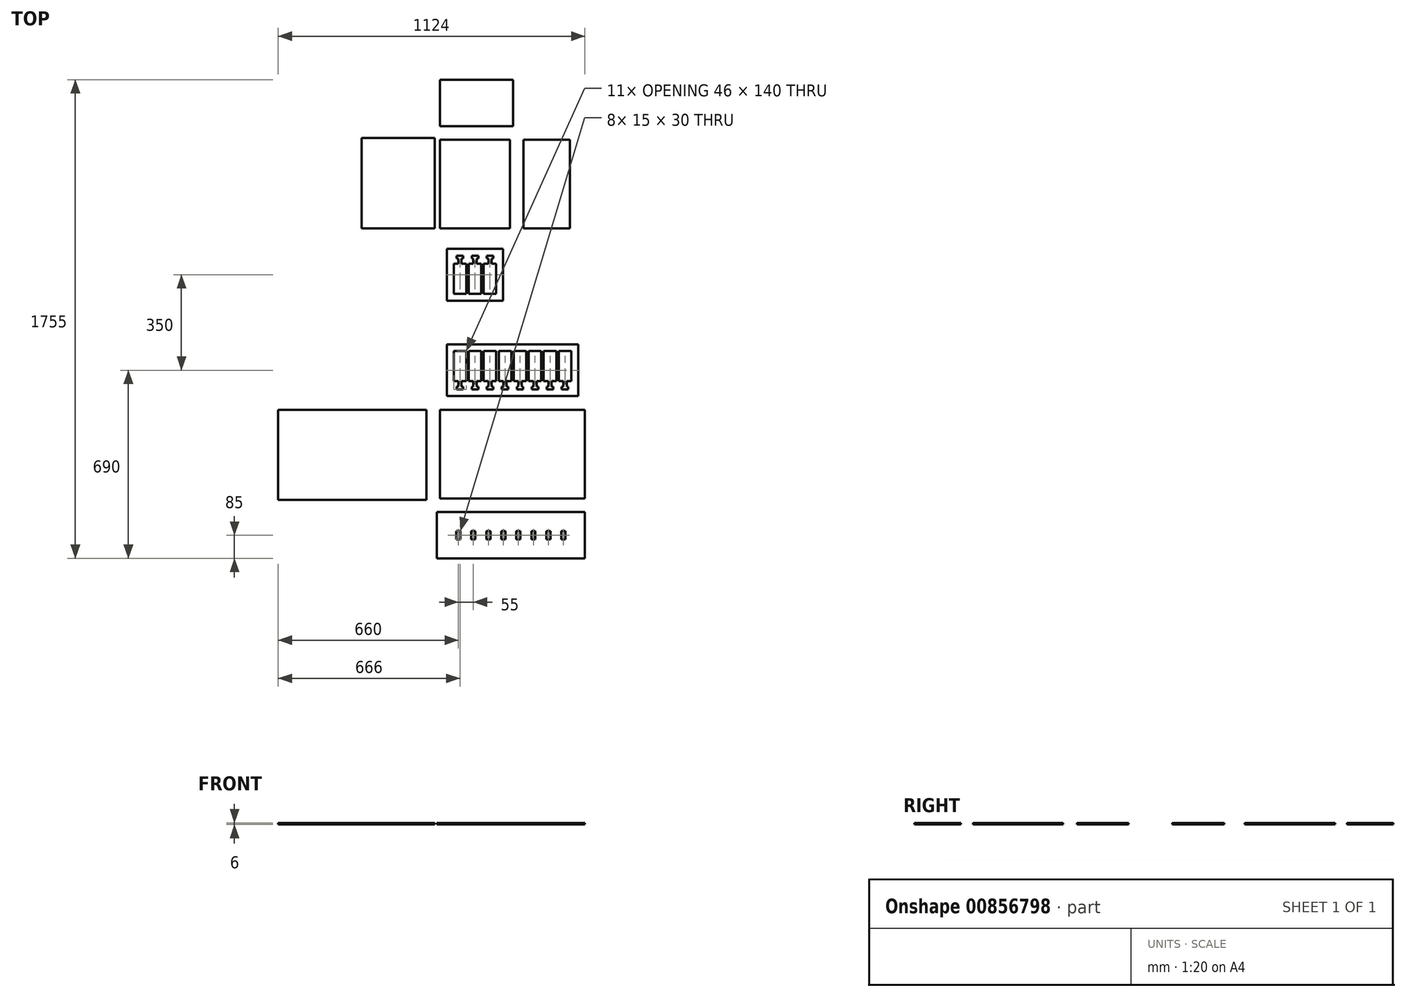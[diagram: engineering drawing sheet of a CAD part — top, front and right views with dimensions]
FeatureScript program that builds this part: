
annotation { "Feature Type Name" : "Feature", "Feature Type Description" : "" }
export const myFeature = defineFeature(function(context is Context, id is Id, definition is map)
    precondition{}
    {
        {
            var Q0;
            Q0=qCreatedBy(makeId("Top.planeOp"),FACE);
            var sketch = newSketch(context, id + "F0", { "sketchPlane" : qUnion([Q0])});
            skLineSegment(sketch, "E0.bottom", {"start": v(0, 0) * mm, "end": v(46, 0) * mm});
            skLineSegment(sketch, "E0.top", {"start": v(0, 110) * mm, "end": v(46, 110) * mm});
            skLineSegment(sketch, "E0.left", {"start": v(0, 0) * mm, "end": v(0, 110) * mm});
            skLineSegment(sketch, "E0.right", {"start": v(46, 0) * mm, "end": v(46, 110) * mm});
            skLineSegment(sketch, "E1.bottom", {"start": v(17, 0) * mm, "end": v(29, 0) * mm});
            skLineSegment(sketch, "E1.top", {"start": v(17, -30) * mm, "end": v(29, -30) * mm});
            skLineSegment(sketch, "E1.left", {"start": v(17, 0) * mm, "end": v(17, -30) * mm});
            skLineSegment(sketch, "E1.right", {"start": v(29, 0) * mm, "end": v(29, -30) * mm});
            skLineSegment(sketch, "E2.1.0.0", {"start": v(101, 0) * mm, "end": v(101, 110) * mm});
            skLineSegment(sketch, "E2.1.0.1", {"start": v(55, 0) * mm, "end": v(55, 110) * mm});
            skLineSegment(sketch, "E2.1.0.2", {"start": v(55, 0) * mm, "end": v(101, 0) * mm});
            skLineSegment(sketch, "E2.1.0.3", {"start": v(55, 110) * mm, "end": v(101, 110) * mm});
            skLineSegment(sketch, "E2.1.0.4", {"start": v(84, 0) * mm, "end": v(84, -30) * mm});
            skLineSegment(sketch, "E2.1.0.5", {"start": v(72, 0) * mm, "end": v(84, 0) * mm});
            skLineSegment(sketch, "E2.1.0.6", {"start": v(72, 0) * mm, "end": v(72, -30) * mm});
            skLineSegment(sketch, "E2.1.0.7", {"start": v(72, -30) * mm, "end": v(84, -30) * mm});
            skLineSegment(sketch, "E2.2.0.0", {"start": v(156, 0) * mm, "end": v(156, 110) * mm});
            skLineSegment(sketch, "E2.2.0.1", {"start": v(110, 0) * mm, "end": v(110, 110) * mm});
            skLineSegment(sketch, "E2.2.0.2", {"start": v(110, 0) * mm, "end": v(156, 0) * mm});
            skLineSegment(sketch, "E2.2.0.3", {"start": v(110, 110) * mm, "end": v(156, 110) * mm});
            skLineSegment(sketch, "E2.2.0.4", {"start": v(139, 0) * mm, "end": v(139, -30) * mm});
            skLineSegment(sketch, "E2.2.0.5", {"start": v(127, 0) * mm, "end": v(139, 0) * mm});
            skLineSegment(sketch, "E2.2.0.6", {"start": v(127, 0) * mm, "end": v(127, -30) * mm});
            skLineSegment(sketch, "E2.2.0.7", {"start": v(127, -30) * mm, "end": v(139, -30) * mm});
            skLineSegment(sketch, "E2.3.0.0", {"start": v(211, 0) * mm, "end": v(211, 110) * mm});
            skLineSegment(sketch, "E2.3.0.1", {"start": v(165, 0) * mm, "end": v(165, 110) * mm});
            skLineSegment(sketch, "E2.3.0.2", {"start": v(165, 0) * mm, "end": v(211, 0) * mm});
            skLineSegment(sketch, "E2.3.0.3", {"start": v(165, 110) * mm, "end": v(211, 110) * mm});
            skLineSegment(sketch, "E2.3.0.4", {"start": v(194, 0) * mm, "end": v(194, -30) * mm});
            skLineSegment(sketch, "E2.3.0.5", {"start": v(182, 0) * mm, "end": v(194, 0) * mm});
            skLineSegment(sketch, "E2.3.0.6", {"start": v(182, 0) * mm, "end": v(182, -30) * mm});
            skLineSegment(sketch, "E2.3.0.7", {"start": v(182, -30) * mm, "end": v(194, -30) * mm});
            skLineSegment(sketch, "E2.4.0.0", {"start": v(266, 0) * mm, "end": v(266, 110) * mm});
            skLineSegment(sketch, "E2.4.0.1", {"start": v(220, 0) * mm, "end": v(220, 110) * mm});
            skLineSegment(sketch, "E2.4.0.2", {"start": v(220, 0) * mm, "end": v(266, 0) * mm});
            skLineSegment(sketch, "E2.4.0.3", {"start": v(220, 110) * mm, "end": v(266, 110) * mm});
            skLineSegment(sketch, "E2.4.0.4", {"start": v(249, 0) * mm, "end": v(249, -30) * mm});
            skLineSegment(sketch, "E2.4.0.5", {"start": v(237, 0) * mm, "end": v(249, 0) * mm});
            skLineSegment(sketch, "E2.4.0.6", {"start": v(237, 0) * mm, "end": v(237, -30) * mm});
            skLineSegment(sketch, "E2.4.0.7", {"start": v(237, -30) * mm, "end": v(249, -30) * mm});
            skLineSegment(sketch, "E2.5.0.0", {"start": v(321, 0) * mm, "end": v(321, 110) * mm});
            skLineSegment(sketch, "E2.5.0.1", {"start": v(275, 0) * mm, "end": v(275, 110) * mm});
            skLineSegment(sketch, "E2.5.0.2", {"start": v(275, 0) * mm, "end": v(321, 0) * mm});
            skLineSegment(sketch, "E2.5.0.3", {"start": v(275, 110) * mm, "end": v(321, 110) * mm});
            skLineSegment(sketch, "E2.5.0.4", {"start": v(304, 0) * mm, "end": v(304, -30) * mm});
            skLineSegment(sketch, "E2.5.0.5", {"start": v(292, 0) * mm, "end": v(304, 0) * mm});
            skLineSegment(sketch, "E2.5.0.6", {"start": v(292, 0) * mm, "end": v(292, -30) * mm});
            skLineSegment(sketch, "E2.5.0.7", {"start": v(292, -30) * mm, "end": v(304, -30) * mm});
            skLineSegment(sketch, "E2.direction1", {"start": v(17, -30) * mm, "end": v(72, -30) * mm, "construction": true});
            skLineSegment(sketch, "E3.bottom", {"start": v(-25, 135) * mm, "end": v(456, 135) * mm});
            skLineSegment(sketch, "E3.top", {"start": v(-25, -55) * mm, "end": v(456, -55) * mm});
            skLineSegment(sketch, "E3.left", {"start": v(-25, 135) * mm, "end": v(-25, -55) * mm});
            skLineSegment(sketch, "E3.right", {"start": v(456, 135) * mm, "end": v(456, -55) * mm});
            skLineSegment(sketch, "E4", {"start": v(-25, -135) * mm, "end": v(-15, -135) * mm, "construction": true});
            skLineSegment(sketch, "E5.MirrorCS", {"start": v(-25, -215) * mm, "end": v(456, -215) * mm, "construction": true});
            skLineSegment(sketch, "E6.MirrorCS", {"start": v(-25, -405) * mm, "end": v(-25, -215) * mm, "construction": true});
            skLineSegment(sketch, "E7.MirrorCS", {"start": v(-25, -405) * mm, "end": v(456, -405) * mm, "construction": true});
            skLineSegment(sketch, "E8.MirrorCS", {"start": v(456, -405) * mm, "end": v(456, -215) * mm, "construction": true});
            skLineSegment(sketch, "E9.bottom", {"start": v(481, -430) * mm, "end": v(-50, -430) * mm});
            skLineSegment(sketch, "E9.top", {"start": v(481, -105) * mm, "end": v(-50, -105) * mm});
            skLineSegment(sketch, "E9.left", {"start": v(481, -430) * mm, "end": v(481, -105) * mm});
            skLineSegment(sketch, "E9.right", {"start": v(-50, -430) * mm, "end": v(-50, -105) * mm});
            skLineSegment(sketch, "E10.bottom", {"start": v(17, -30) * mm, "end": v(11, -30) * mm});
            skLineSegment(sketch, "E10.top", {"start": v(17, -20) * mm, "end": v(11, -20) * mm});
            skLineSegment(sketch, "E10.left", {"start": v(17, -30) * mm, "end": v(17, -20) * mm});
            skLineSegment(sketch, "E10.right", {"start": v(11, -30) * mm, "end": v(11, -20) * mm});
            skLineSegment(sketch, "E11", {"start": v(23, -30) * mm, "end": v(23, -20) * mm, "construction": true});
            skLineSegment(sketch, "E12.MirrorCS", {"start": v(29, -20) * mm, "end": v(35, -20) * mm});
            skLineSegment(sketch, "E13.MirrorCS", {"start": v(35, -30) * mm, "end": v(35, -20) * mm});
            skLineSegment(sketch, "E14.MirrorCS", {"start": v(29, -30) * mm, "end": v(35, -30) * mm});
            skLineSegment(sketch, "E15.1.0.0", {"start": v(72, -20) * mm, "end": v(66, -20) * mm});
            skLineSegment(sketch, "E15.1.0.1", {"start": v(66, -30) * mm, "end": v(66, -20) * mm});
            skLineSegment(sketch, "E15.1.0.2", {"start": v(72, -30) * mm, "end": v(66, -30) * mm});
            skLineSegment(sketch, "E15.1.0.3", {"start": v(84, -20) * mm, "end": v(90, -20) * mm});
            skLineSegment(sketch, "E15.1.0.4", {"start": v(90, -30) * mm, "end": v(90, -20) * mm});
            skLineSegment(sketch, "E15.1.0.5", {"start": v(84, -30) * mm, "end": v(90, -30) * mm});
            skLineSegment(sketch, "E15.2.0.0", {"start": v(127, -20) * mm, "end": v(121, -20) * mm});
            skLineSegment(sketch, "E15.2.0.1", {"start": v(121, -30) * mm, "end": v(121, -20) * mm});
            skLineSegment(sketch, "E15.2.0.2", {"start": v(127, -30) * mm, "end": v(121, -30) * mm});
            skLineSegment(sketch, "E15.2.0.3", {"start": v(139, -20) * mm, "end": v(145, -20) * mm});
            skLineSegment(sketch, "E15.2.0.4", {"start": v(145, -30) * mm, "end": v(145, -20) * mm});
            skLineSegment(sketch, "E15.2.0.5", {"start": v(139, -30) * mm, "end": v(145, -30) * mm});
            skLineSegment(sketch, "E15.3.0.0", {"start": v(182, -20) * mm, "end": v(176, -20) * mm});
            skLineSegment(sketch, "E15.3.0.1", {"start": v(176, -30) * mm, "end": v(176, -20) * mm});
            skLineSegment(sketch, "E15.3.0.2", {"start": v(182, -30) * mm, "end": v(176, -30) * mm});
            skLineSegment(sketch, "E15.3.0.3", {"start": v(194, -20) * mm, "end": v(200, -20) * mm});
            skLineSegment(sketch, "E15.3.0.4", {"start": v(200, -30) * mm, "end": v(200, -20) * mm});
            skLineSegment(sketch, "E15.3.0.5", {"start": v(194, -30) * mm, "end": v(200, -30) * mm});
            skLineSegment(sketch, "E15.4.0.0", {"start": v(237, -20) * mm, "end": v(231, -20) * mm});
            skLineSegment(sketch, "E15.4.0.1", {"start": v(231, -30) * mm, "end": v(231, -20) * mm});
            skLineSegment(sketch, "E15.4.0.2", {"start": v(237, -30) * mm, "end": v(231, -30) * mm});
            skLineSegment(sketch, "E15.4.0.3", {"start": v(249, -20) * mm, "end": v(255, -20) * mm});
            skLineSegment(sketch, "E15.4.0.4", {"start": v(255, -30) * mm, "end": v(255, -20) * mm});
            skLineSegment(sketch, "E15.4.0.5", {"start": v(249, -30) * mm, "end": v(255, -30) * mm});
            skLineSegment(sketch, "E15.5.0.0", {"start": v(292, -20) * mm, "end": v(286, -20) * mm});
            skLineSegment(sketch, "E15.5.0.1", {"start": v(286, -30) * mm, "end": v(286, -20) * mm});
            skLineSegment(sketch, "E15.5.0.2", {"start": v(292, -30) * mm, "end": v(286, -30) * mm});
            skLineSegment(sketch, "E15.5.0.3", {"start": v(304, -20) * mm, "end": v(310, -20) * mm});
            skLineSegment(sketch, "E15.5.0.4", {"start": v(310, -30) * mm, "end": v(310, -20) * mm});
            skLineSegment(sketch, "E15.5.0.5", {"start": v(304, -30) * mm, "end": v(310, -30) * mm});
            skLineSegment(sketch, "E15.direction1", {"start": v(11, -20) * mm, "end": v(66, -20) * mm, "construction": true});
            skLineSegment(sketch, "E16", {"start": v(-25, 40) * mm, "end": v(-15, 40) * mm, "construction": true});
            skLineSegment(sketch, "E17.MirrorCS", {"start": v(-25, 215) * mm, "end": v(-15, 215) * mm, "construction": true});
            skLineSegment(sketch, "E18.MirrorCS", {"start": v(-25, 295) * mm, "end": v(-25, 485) * mm});
            skLineSegment(sketch, "E19.MirrorCS", {"start": v(84, 460) * mm, "end": v(90, 460) * mm});
            skLineSegment(sketch, "E20.MirrorCS", {"start": v(17, 450) * mm, "end": v(11, 450) * mm});
            skLineSegment(sketch, "E21.MirrorCS", {"start": v(29, 460) * mm, "end": v(35, 460) * mm});
            skLineSegment(sketch, "E22.MirrorCS", {"start": v(139, 460) * mm, "end": v(145, 460) * mm});
            skLineSegment(sketch, "E23.MirrorCS", {"start": v(127, 460) * mm, "end": v(121, 460) * mm});
            skLineSegment(sketch, "E24.MirrorCS", {"start": v(17, 460) * mm, "end": v(11, 460) * mm});
            skLineSegment(sketch, "E25.MirrorCS", {"start": v(72, 460) * mm, "end": v(66, 460) * mm});
            skLineSegment(sketch, "E26.MirrorCS", {"start": v(29, 450) * mm, "end": v(35, 450) * mm});
            skLineSegment(sketch, "E27.MirrorCS", {"start": v(127, 450) * mm, "end": v(121, 450) * mm});
            skLineSegment(sketch, "E28.MirrorCS", {"start": v(72, 430) * mm, "end": v(84, 430) * mm});
            skLineSegment(sketch, "E29.MirrorCS", {"start": v(17, 460) * mm, "end": v(29, 460) * mm});
            skLineSegment(sketch, "E30.MirrorCS", {"start": v(84, 450) * mm, "end": v(90, 450) * mm});
            skLineSegment(sketch, "E31.MirrorCS", {"start": v(139, 450) * mm, "end": v(145, 450) * mm});
            skLineSegment(sketch, "E32.MirrorCS", {"start": v(17, 460) * mm, "end": v(17, 450) * mm});
            skLineSegment(sketch, "E33.MirrorCS", {"start": v(72, 460) * mm, "end": v(84, 460) * mm});
            skLineSegment(sketch, "E34.MirrorCS", {"start": v(84, 430) * mm, "end": v(84, 460) * mm});
            skLineSegment(sketch, "E35.MirrorCS", {"start": v(101, 430) * mm, "end": v(101, 320) * mm});
            skLineSegment(sketch, "E36.MirrorCS", {"start": v(11, 460) * mm, "end": v(11, 450) * mm});
            skLineSegment(sketch, "E37.MirrorCS", {"start": v(156, 430) * mm, "end": v(156, 320) * mm});
            skLineSegment(sketch, "E38.MirrorCS", {"start": v(110, 430) * mm, "end": v(110, 320) * mm});
            skLineSegment(sketch, "E39.MirrorCS", {"start": v(55, 320) * mm, "end": v(101, 320) * mm});
            skLineSegment(sketch, "E40.MirrorCS", {"start": v(110, 320) * mm, "end": v(156, 320) * mm});
            skLineSegment(sketch, "E41.MirrorCS", {"start": v(127, 430) * mm, "end": v(139, 430) * mm});
            skLineSegment(sketch, "E42.MirrorCS", {"start": v(66, 460) * mm, "end": v(66, 450) * mm});
            skLineSegment(sketch, "E43.MirrorCS", {"start": v(72, 430) * mm, "end": v(72, 460) * mm});
            skLineSegment(sketch, "E44.MirrorCS", {"start": v(17, 430) * mm, "end": v(29, 430) * mm});
            skLineSegment(sketch, "E45.MirrorCS", {"start": v(17, 460) * mm, "end": v(72, 460) * mm, "construction": true});
            skLineSegment(sketch, "E46.MirrorCS", {"start": v(23, 460) * mm, "end": v(23, 450) * mm, "construction": true});
            skLineSegment(sketch, "E47.MirrorCS", {"start": v(0, 430) * mm, "end": v(46, 430) * mm});
            skLineSegment(sketch, "E48.MirrorCS", {"start": v(110, 430) * mm, "end": v(156, 430) * mm});
            skLineSegment(sketch, "E49.MirrorCS", {"start": v(145, 460) * mm, "end": v(145, 450) * mm});
            skLineSegment(sketch, "E50.MirrorCS", {"start": v(127, 460) * mm, "end": v(139, 460) * mm});
            skLineSegment(sketch, "E51.MirrorCS", {"start": v(0, 430) * mm, "end": v(0, 320) * mm});
            skLineSegment(sketch, "E52.MirrorCS", {"start": v(55, 430) * mm, "end": v(55, 320) * mm});
            skLineSegment(sketch, "E53.MirrorCS", {"start": v(0, 320) * mm, "end": v(46, 320) * mm});
            skLineSegment(sketch, "E54.MirrorCS", {"start": v(46, 430) * mm, "end": v(46, 320) * mm});
            skLineSegment(sketch, "E55.MirrorCS", {"start": v(121, 460) * mm, "end": v(121, 450) * mm});
            skLineSegment(sketch, "E56.MirrorCS", {"start": v(55, 430) * mm, "end": v(101, 430) * mm});
            skLineSegment(sketch, "E57.MirrorCS", {"start": v(11, 450) * mm, "end": v(66, 450) * mm, "construction": true});
            skLineSegment(sketch, "E58.MirrorCS", {"start": v(139, 430) * mm, "end": v(139, 460) * mm});
            skLineSegment(sketch, "E59.MirrorCS", {"start": v(72, 450) * mm, "end": v(66, 450) * mm});
            skLineSegment(sketch, "E60.MirrorCS", {"start": v(90, 460) * mm, "end": v(90, 450) * mm});
            skLineSegment(sketch, "E61.MirrorCS", {"start": v(127, 430) * mm, "end": v(127, 460) * mm});
            skLineSegment(sketch, "E62.MirrorCS", {"start": v(35, 460) * mm, "end": v(35, 450) * mm});
            skLineSegment(sketch, "E63.MirrorCS", {"start": v(17, 430) * mm, "end": v(17, 460) * mm});
            skLineSegment(sketch, "E64.MirrorCS", {"start": v(29, 430) * mm, "end": v(29, 460) * mm});
            skLineSegment(sketch, "E65", {"start": v(-25, 485) * mm, "end": v(181, 485) * mm});
            skLineSegment(sketch, "E66", {"start": v(181, 485) * mm, "end": v(181, 295) * mm});
            skLineSegment(sketch, "E67", {"start": v(181, 295) * mm, "end": v(-25, 295) * mm});
            skLineSegment(sketch, "E68", {"start": v(-25, 535) * mm, "end": v(0, 535) * mm, "construction": true});
            skLineSegment(sketch, "E69.MirrorCS", {"start": v(-25, 585) * mm, "end": v(181, 585) * mm, "construction": true});
            skLineSegment(sketch, "E70.MirrorCS", {"start": v(-25, 775) * mm, "end": v(-25, 585) * mm, "construction": true});
            skLineSegment(sketch, "E71.MirrorCS", {"start": v(181, 775) * mm, "end": v(-25, 775) * mm, "construction": true});
            skLineSegment(sketch, "E72.MirrorCS", {"start": v(181, 585) * mm, "end": v(181, 775) * mm, "construction": true});
            skLineSegment(sketch, "E73.bottom", {"start": v(-50, 560) * mm, "end": v(206, 560) * mm});
            skLineSegment(sketch, "E73.top", {"start": v(-50, 885) * mm, "end": v(206, 885) * mm});
            skLineSegment(sketch, "E73.left", {"start": v(-50, 560) * mm, "end": v(-50, 885) * mm});
            skLineSegment(sketch, "E73.right", {"start": v(206, 560) * mm, "end": v(206, 885) * mm});
            skLineSegment(sketch, "E74.bottom", {"start": v(256, 560) * mm, "end": v(426, 560) * mm});
            skLineSegment(sketch, "E74.top", {"start": v(256, 885) * mm, "end": v(426, 885) * mm});
            skLineSegment(sketch, "E74.left", {"start": v(256, 560) * mm, "end": v(256, 885) * mm});
            skLineSegment(sketch, "E74.right", {"start": v(426, 560) * mm, "end": v(426, 885) * mm});
            skLineSegment(sketch, "E75.left", {"start": v(-50, 935) * mm, "end": v(-50, 1105) * mm});
            skLineSegment(sketch, "E75.right", {"start": v(218, 935) * mm, "end": v(218, 1105) * mm});
            skLineSegment(sketch, "E76", {"start": v(-50, 1105) * mm, "end": v(218, 1105) * mm});
            skLineSegment(sketch, "E77", {"start": v(-50, 935) * mm, "end": v(218, 935) * mm});
            skLineSegment(sketch, "E78.bottom", {"start": v(-70, 560) * mm, "end": v(-338, 560) * mm});
            skLineSegment(sketch, "E78.top", {"start": v(-70, 891) * mm, "end": v(-338, 891) * mm});
            skLineSegment(sketch, "E78.left", {"start": v(-70, 560) * mm, "end": v(-70, 891) * mm});
            skLineSegment(sketch, "E78.right", {"start": v(-338, 560) * mm, "end": v(-338, 891) * mm});
            skLineSegment(sketch, "E79.bottom", {"start": v(481, -480) * mm, "end": v(-62, -480) * mm});
            skLineSegment(sketch, "E79.top", {"start": v(481, -650) * mm, "end": v(-62, -650) * mm});
            skLineSegment(sketch, "E79.left", {"start": v(481, -480) * mm, "end": v(481, -650) * mm});
            skLineSegment(sketch, "E79.right", {"start": v(-62, -480) * mm, "end": v(-62, -650) * mm});
            skLineSegment(sketch, "E80.bottom", {"start": v(-100, -105) * mm, "end": v(-643, -105) * mm});
            skLineSegment(sketch, "E80.top", {"start": v(-100, -436) * mm, "end": v(-643, -436) * mm});
            skLineSegment(sketch, "E80.left", {"start": v(-100, -105) * mm, "end": v(-100, -436) * mm});
            skLineSegment(sketch, "E80.right", {"start": v(-643, -105) * mm, "end": v(-643, -436) * mm});
            skLineSegment(sketch, "E81.bottom", {"start": v(450, -644) * mm, "end": v(-31, -644) * mm, "construction": true});
            skLineSegment(sketch, "E81.top", {"start": v(450, -486) * mm, "end": v(-31, -486) * mm, "construction": true});
            skLineSegment(sketch, "E81.left", {"start": v(450, -644) * mm, "end": v(450, -486) * mm, "construction": true});
            skLineSegment(sketch, "E81.right", {"start": v(-31, -644) * mm, "end": v(-31, -486) * mm, "construction": true});
            skLineSegment(sketch, "E82", {"start": v(17, -486) * mm, "end": v(17, -644) * mm, "construction": true});
            skLineSegment(sketch, "E83.1.0.0", {"start": v(72, -486) * mm, "end": v(72, -644) * mm, "construction": true});
            skLineSegment(sketch, "E83.2.0.0", {"start": v(127, -486) * mm, "end": v(127, -644) * mm, "construction": true});
            skLineSegment(sketch, "E83.3.0.0", {"start": v(182, -486) * mm, "end": v(182, -644) * mm, "construction": true});
            skLineSegment(sketch, "E83.4.0.0", {"start": v(237, -486) * mm, "end": v(237, -644) * mm, "construction": true});
            skLineSegment(sketch, "E83.5.0.0", {"start": v(292, -486) * mm, "end": v(292, -644) * mm, "construction": true});
            skLineSegment(sketch, "E83.direction1", {"start": v(17, -644) * mm, "end": v(72, -644) * mm, "construction": true});
            skLineSegment(sketch, "E84.bottom", {"start": v(9.5, -550) * mm, "end": v(24.5, -550) * mm});
            skLineSegment(sketch, "E84.top", {"start": v(9.5, -580) * mm, "end": v(24.5, -580) * mm});
            skLineSegment(sketch, "E84.left", {"start": v(9.5, -550) * mm, "end": v(9.5, -580) * mm});
            skLineSegment(sketch, "E84.right", {"start": v(24.5, -550) * mm, "end": v(24.5, -580) * mm});
            skPoint(sketch, "E84.middle", {"position": v(17, -565) * mm});
            skLineSegment(sketch, "E85.1.0.0", {"start": v(64.5, -550) * mm, "end": v(79.5, -550) * mm});
            skLineSegment(sketch, "E85.1.0.1", {"start": v(64.5, -580) * mm, "end": v(79.5, -580) * mm});
            skLineSegment(sketch, "E85.1.0.2", {"start": v(79.5, -550) * mm, "end": v(79.5, -580) * mm});
            skLineSegment(sketch, "E85.1.0.3", {"start": v(64.5, -550) * mm, "end": v(64.5, -580) * mm});
            skPoint(sketch, "E85.1.0.4", {"position": v(72, -565) * mm});
            skLineSegment(sketch, "E85.2.0.0", {"start": v(119.5, -550) * mm, "end": v(134.5, -550) * mm});
            skLineSegment(sketch, "E85.2.0.1", {"start": v(119.5, -580) * mm, "end": v(134.5, -580) * mm});
            skLineSegment(sketch, "E85.2.0.2", {"start": v(134.5, -550) * mm, "end": v(134.5, -580) * mm});
            skLineSegment(sketch, "E85.2.0.3", {"start": v(119.5, -550) * mm, "end": v(119.5, -580) * mm});
            skPoint(sketch, "E85.2.0.4", {"position": v(127, -565) * mm});
            skLineSegment(sketch, "E85.3.0.0", {"start": v(174.5, -550) * mm, "end": v(189.5, -550) * mm});
            skLineSegment(sketch, "E85.3.0.1", {"start": v(174.5, -580) * mm, "end": v(189.5, -580) * mm});
            skLineSegment(sketch, "E85.3.0.2", {"start": v(189.5, -550) * mm, "end": v(189.5, -580) * mm});
            skLineSegment(sketch, "E85.3.0.3", {"start": v(174.5, -550) * mm, "end": v(174.5, -580) * mm});
            skPoint(sketch, "E85.3.0.4", {"position": v(182, -565) * mm});
            skLineSegment(sketch, "E85.4.0.0", {"start": v(229.5, -550) * mm, "end": v(244.5, -550) * mm});
            skLineSegment(sketch, "E85.4.0.1", {"start": v(229.5, -580) * mm, "end": v(244.5, -580) * mm});
            skLineSegment(sketch, "E85.4.0.2", {"start": v(244.5, -550) * mm, "end": v(244.5, -580) * mm});
            skLineSegment(sketch, "E85.4.0.3", {"start": v(229.5, -550) * mm, "end": v(229.5, -580) * mm});
            skPoint(sketch, "E85.4.0.4", {"position": v(237, -565) * mm});
            skLineSegment(sketch, "E85.5.0.0", {"start": v(284.5, -550) * mm, "end": v(299.5, -550) * mm});
            skLineSegment(sketch, "E85.5.0.1", {"start": v(284.5, -580) * mm, "end": v(299.5, -580) * mm});
            skLineSegment(sketch, "E85.5.0.2", {"start": v(299.5, -550) * mm, "end": v(299.5, -580) * mm});
            skLineSegment(sketch, "E85.5.0.3", {"start": v(284.5, -550) * mm, "end": v(284.5, -580) * mm});
            skPoint(sketch, "E85.5.0.4", {"position": v(292, -565) * mm});
            skLineSegment(sketch, "E85.direction1", {"start": v(9.5, -580) * mm, "end": v(64.5, -580) * mm, "construction": true});
            skLineSegment(sketch, "E86.0.6.0", {"start": v(376, 0) * mm, "end": v(376, 110) * mm});
            skLineSegment(sketch, "E86.3.6.0", {"start": v(330, 0) * mm, "end": v(330, 110) * mm});
            skLineSegment(sketch, "E86.6.6.0", {"start": v(330, 0) * mm, "end": v(376, 0) * mm});
            skLineSegment(sketch, "E86.9.6.0", {"start": v(330, 110) * mm, "end": v(376, 110) * mm});
            skLineSegment(sketch, "E86.12.6.0", {"start": v(359, 0) * mm, "end": v(359, -30) * mm});
            skLineSegment(sketch, "E86.15.6.0", {"start": v(347, 0) * mm, "end": v(359, 0) * mm});
            skLineSegment(sketch, "E86.18.6.0", {"start": v(347, 0) * mm, "end": v(347, -30) * mm});
            skLineSegment(sketch, "E86.21.6.0", {"start": v(347, -30) * mm, "end": v(359, -30) * mm});
            skLineSegment(sketch, "E86.0.7.0", {"start": v(431, 0) * mm, "end": v(431, 110) * mm});
            skLineSegment(sketch, "E86.3.7.0", {"start": v(385, 0) * mm, "end": v(385, 110) * mm});
            skLineSegment(sketch, "E86.6.7.0", {"start": v(385, 0) * mm, "end": v(431, 0) * mm});
            skLineSegment(sketch, "E86.9.7.0", {"start": v(385, 110) * mm, "end": v(431, 110) * mm});
            skLineSegment(sketch, "E86.12.7.0", {"start": v(414, 0) * mm, "end": v(414, -30) * mm});
            skLineSegment(sketch, "E86.15.7.0", {"start": v(402, 0) * mm, "end": v(414, 0) * mm});
            skLineSegment(sketch, "E86.18.7.0", {"start": v(402, 0) * mm, "end": v(402, -30) * mm});
            skLineSegment(sketch, "E86.21.7.0", {"start": v(402, -30) * mm, "end": v(414, -30) * mm});
            skLineSegment(sketch, "E87.0.6.0", {"start": v(347, -20) * mm, "end": v(341, -20) * mm});
            skLineSegment(sketch, "E87.3.6.0", {"start": v(341, -30) * mm, "end": v(341, -20) * mm});
            skLineSegment(sketch, "E87.6.6.0", {"start": v(347, -30) * mm, "end": v(341, -30) * mm});
            skLineSegment(sketch, "E87.9.6.0", {"start": v(359, -20) * mm, "end": v(365, -20) * mm});
            skLineSegment(sketch, "E87.12.6.0", {"start": v(365, -30) * mm, "end": v(365, -20) * mm});
            skLineSegment(sketch, "E87.15.6.0", {"start": v(359, -30) * mm, "end": v(365, -30) * mm});
            skLineSegment(sketch, "E87.0.7.0", {"start": v(402, -20) * mm, "end": v(396, -20) * mm});
            skLineSegment(sketch, "E87.3.7.0", {"start": v(396, -30) * mm, "end": v(396, -20) * mm});
            skLineSegment(sketch, "E87.6.7.0", {"start": v(402, -30) * mm, "end": v(396, -30) * mm});
            skLineSegment(sketch, "E87.9.7.0", {"start": v(414, -20) * mm, "end": v(420, -20) * mm});
            skLineSegment(sketch, "E87.12.7.0", {"start": v(420, -30) * mm, "end": v(420, -20) * mm});
            skLineSegment(sketch, "E87.15.7.0", {"start": v(414, -30) * mm, "end": v(420, -30) * mm});
            skLineSegment(sketch, "E88.0.6.0", {"start": v(347, -486) * mm, "end": v(347, -644) * mm, "construction": true});
            skLineSegment(sketch, "E88.0.7.0", {"start": v(402, -486) * mm, "end": v(402, -644) * mm, "construction": true});
            skLineSegment(sketch, "E89.0.6.0", {"start": v(339.5, -550) * mm, "end": v(354.5, -550) * mm});
            skLineSegment(sketch, "E89.3.6.0", {"start": v(339.5, -580) * mm, "end": v(354.5, -580) * mm});
            skLineSegment(sketch, "E89.6.6.0", {"start": v(354.5, -550) * mm, "end": v(354.5, -580) * mm});
            skLineSegment(sketch, "E89.9.6.0", {"start": v(339.5, -550) * mm, "end": v(339.5, -580) * mm});
            skPoint(sketch, "E89.12.6.0", {"position": v(347, -565) * mm});
            skLineSegment(sketch, "E89.0.7.0", {"start": v(394.5, -550) * mm, "end": v(409.5, -550) * mm});
            skLineSegment(sketch, "E89.3.7.0", {"start": v(394.5, -580) * mm, "end": v(409.5, -580) * mm});
            skLineSegment(sketch, "E89.6.7.0", {"start": v(409.5, -550) * mm, "end": v(409.5, -580) * mm});
            skLineSegment(sketch, "E89.9.7.0", {"start": v(394.5, -550) * mm, "end": v(394.5, -580) * mm});
            skPoint(sketch, "E89.12.7.0", {"position": v(402, -565) * mm});
            skSolve(sketch);
        }
        {
            var Q0;
            Q0=makeQuery(id+"F0.imprint","IMPRINT",FACE,{"disambiguationData":[TD([[makeQuery(id+"F0.imprint","IMPRINT",EDGE,{"derivedFrom":sQuery(id+"F0.wireOp",EDGE,"E0.top")}),1.0]])]});
            var Q1;
            Q1=makeQuery(id+"F0.imprint","IMPRINT",FACE,{"disambiguationData":[TD([[makeQuery(id+"F0.imprint","IMPRINT",EDGE,{"derivedFrom":sQuery(id+"F0.wireOp",EDGE,"E18.MirrorCS")}),-1.0]])]});
            extrude(context, id + "F1", {"entities" : qUnion([Q0, Q1]), "depth" : 6 * mm, "offsetDistance" : 25 * mm});
        }
        {
            var Q0;
            Q0=makeQuery(id+"F0.imprint","IMPRINT",FACE,{"disambiguationData":[TD([[makeQuery(id+"F0.imprint","IMPRINT",EDGE,{"derivedFrom":sQuery(id+"F0.wireOp",EDGE,"E9.bottom")}),-1.0]])]});
            var Q1;
            Q1=makeQuery(id+"F0.imprint","IMPRINT",FACE,{"disambiguationData":[TD([[makeQuery(id+"F0.imprint","IMPRINT",EDGE,{"derivedFrom":sQuery(id+"F0.wireOp",EDGE,"E73.bottom")}),1.0]])]});
            var Q2;
            Q2=makeQuery(id+"F0.imprint","IMPRINT",FACE,{"disambiguationData":[TD([[makeQuery(id+"F0.imprint","IMPRINT",EDGE,{"derivedFrom":sQuery(id+"F0.wireOp",EDGE,"E74.bottom")}),1.0]])]});
            var Q3;
            Q3=makeQuery(id+"F0.imprint","IMPRINT",FACE,{"disambiguationData":[TD([[makeQuery(id+"F0.imprint","IMPRINT",EDGE,{"derivedFrom":sQuery(id+"F0.wireOp",EDGE,"E75.bottom")}),1.0]])]});
            var Q4;
            Q4=makeQuery(id+"F0.imprint","IMPRINT",FACE,{"disambiguationData":[TD([[makeQuery(id+"F0.imprint","IMPRINT",EDGE,{"derivedFrom":sQuery(id+"F0.wireOp",EDGE,"E75.left")}),-1.0]])]});
            var Q5;
            Q5=makeQuery(id+"F0.imprint","IMPRINT",FACE,{"disambiguationData":[TD([[makeQuery(id+"F0.imprint","IMPRINT",EDGE,{"derivedFrom":sQuery(id+"F0.wireOp",EDGE,"E78.bottom")}),-1.0]])]});
            var Q6;
            Q6=makeQuery(id+"F0.imprint","IMPRINT",FACE,{"disambiguationData":[TD([[makeQuery(id+"F0.imprint","IMPRINT",EDGE,{"derivedFrom":sQuery(id+"F0.wireOp",EDGE,"E79.bottom")}),1.0]])]});
            var Q7;
            Q7=makeQuery(id+"F0.imprint","IMPRINT",FACE,{"disambiguationData":[TD([[makeQuery(id+"F0.imprint","IMPRINT",EDGE,{"derivedFrom":sQuery(id+"F0.wireOp",EDGE,"E80.bottom")}),1.0]])]});
            extrude(context, id + "F2", {"entities" : qUnion([Q0, Q1, Q2, Q3, Q4, Q5, Q6, Q7]), "depth" : 6 * mm, "offsetDistance" : 25 * mm});
        }
    });
